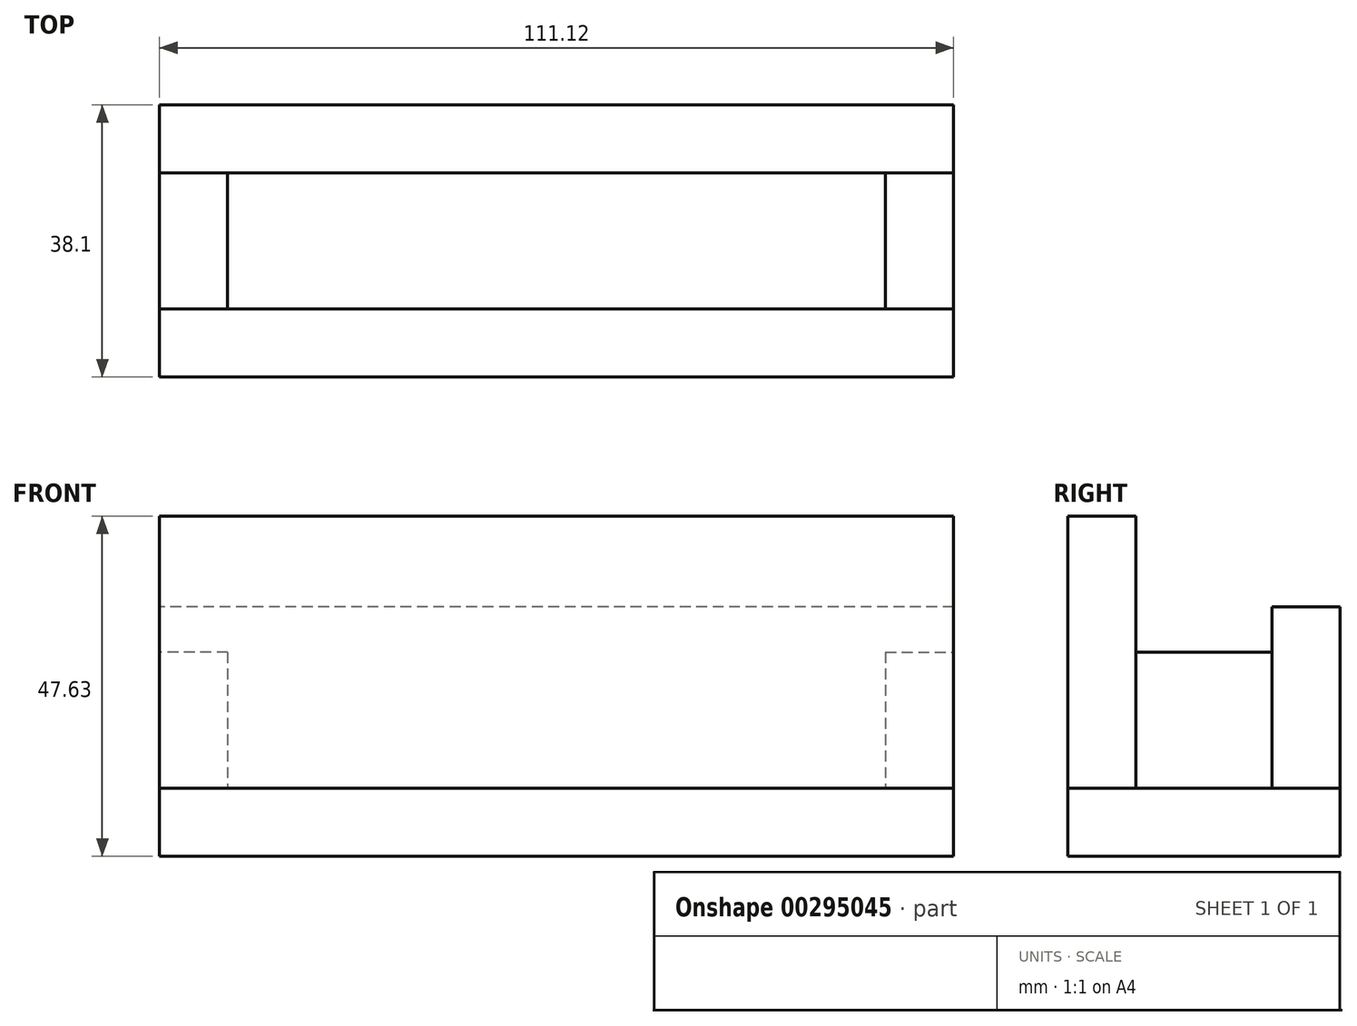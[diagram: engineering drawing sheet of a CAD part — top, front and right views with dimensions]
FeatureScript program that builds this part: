
annotation { "Feature Type Name" : "Feature", "Feature Type Description" : "" }
export const myFeature = defineFeature(function(context is Context, id is Id, definition is map)
    precondition{}
    {
        {
            var Q0;
            Q0=qCreatedBy(makeId("Top.planeOp"),FACE);
            var sketch = newSketch(context, id + "F0", { "sketchPlane" : qUnion([Q0])});
            skLineSegment(sketch, "E0.bottom", {"start": v(-46.04, -9.52) * mm, "end": v(46.04, -9.52) * mm});
            skLineSegment(sketch, "E0.top", {"start": v(-46.04, 9.53) * mm, "end": v(46.04, 9.53) * mm});
            skLineSegment(sketch, "E0.left", {"start": v(-46.04, -9.52) * mm, "end": v(-46.04, 9.53) * mm});
            skLineSegment(sketch, "E0.right", {"start": v(46.04, -9.52) * mm, "end": v(46.04, 9.53) * mm});
            skPoint(sketch, "E0.middle", {"position": v(0, 0) * mm});
            skLineSegment(sketch, "E1.bottom", {"start": v(-55.56, -19.05) * mm, "end": v(55.56, -19.05) * mm});
            skLineSegment(sketch, "E1.top", {"start": v(-55.56, 19.05) * mm, "end": v(55.56, 19.05) * mm});
            skLineSegment(sketch, "E1.left", {"start": v(-55.56, -19.05) * mm, "end": v(-55.56, 19.05) * mm});
            skLineSegment(sketch, "E1.right", {"start": v(55.56, -19.05) * mm, "end": v(55.56, 19.05) * mm});
            skLineSegment(sketch, "E2", {"start": v(46.04, 9.53) * mm, "end": v(55.56, 9.53) * mm});
            skLineSegment(sketch, "E3", {"start": v(46.04, -9.52) * mm, "end": v(55.56, -9.52) * mm});
            skLineSegment(sketch, "E4", {"start": v(-46.04, -9.52) * mm, "end": v(-55.56, -9.52) * mm});
            skLineSegment(sketch, "E5", {"start": v(-46.04, 9.53) * mm, "end": v(-55.56, 9.53) * mm});
            skSolve(sketch);
        }
        {
            var Q0;
            Q0=makeQuery(id+"F0.imprint","IMPRINT",FACE,{"disambiguationData":[TD([[makeQuery(id+"F0.imprint","IMPRINT",EDGE,{"derivedFrom":sQuery(id+"F0.wireOp",EDGE,"E0.bottom")}),1.0]])]});
            var Q1;
            Q1=makeQuery(id+"F0.imprint","IMPRINT",FACE,{"disambiguationData":[TD([[makeQuery(id+"F0.imprint","IMPRINT",EDGE,{"derivedFrom":sQuery(id+"F0.wireOp",EDGE,"E0.bottom")}),-1.0]])]});
            var Q2;
            Q2=makeQuery(id+"F0.imprint","IMPRINT",FACE,{"disambiguationData":[TD([[makeQuery(id+"F0.imprint","IMPRINT",EDGE,{"derivedFrom":sQuery(id+"F0.wireOp",EDGE,"E0.right")}),-1.0]])]});
            var Q3;
            Q3=makeQuery(id+"F0.imprint","IMPRINT",FACE,{"disambiguationData":[TD([[makeQuery(id+"F0.imprint","IMPRINT",EDGE,{"derivedFrom":sQuery(id+"F0.wireOp",EDGE,"E0.top")}),1.0]])]});
            var Q4;
            Q4=makeQuery(id+"F0.imprint","IMPRINT",FACE,{"disambiguationData":[TD([[makeQuery(id+"F0.imprint","IMPRINT",EDGE,{"derivedFrom":sQuery(id+"F0.wireOp",EDGE,"E0.left")}),1.0]])]});
            extrude(context, id + "F1", {"entities" : qUnion([Q0, Q1, Q2, Q3, Q4]), "oppositeDirection" : true, "depth" : 9.52 * mm});
        }
        {
            var Q0;
            Q0=makeQuery(id+"F0.imprint","IMPRINT",FACE,{"disambiguationData":[TD([[makeQuery(id+"F0.imprint","IMPRINT",EDGE,{"derivedFrom":sQuery(id+"F0.wireOp",EDGE,"E0.right")}),-1.0]])]});
            var Q1;
            Q1=makeQuery(id+"F0.imprint","IMPRINT",FACE,{"disambiguationData":[TD([[makeQuery(id+"F0.imprint","IMPRINT",EDGE,{"derivedFrom":sQuery(id+"F0.wireOp",EDGE,"E0.left")}),1.0]])]});
            extrude(context, id + "F2", {"entities" : qUnion([Q0, Q1]), "depth" : 19.05 * mm});
        }
        {
            var Q0;
            Q0=makeQuery(id+"F0.imprint","IMPRINT",FACE,{"disambiguationData":[TD([[makeQuery(id+"F0.imprint","IMPRINT",EDGE,{"derivedFrom":sQuery(id+"F0.wireOp",EDGE,"E0.top")}),1.0]])]});
            extrude(context, id + "F3", {"entities" : qUnion([Q0]), "depth" : 25.4 * mm});
        }
        {
            var Q0;
            Q0=makeQuery(id+"F0.imprint","IMPRINT",FACE,{"disambiguationData":[TD([[makeQuery(id+"F0.imprint","IMPRINT",EDGE,{"derivedFrom":sQuery(id+"F0.wireOp",EDGE,"E0.bottom")}),-1.0]])]});
            extrude(context, id + "F4", {"entities" : qUnion([Q0]), "depth" : 38.1 * mm});
        }
    });
